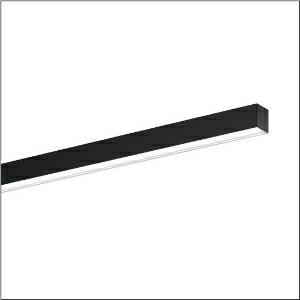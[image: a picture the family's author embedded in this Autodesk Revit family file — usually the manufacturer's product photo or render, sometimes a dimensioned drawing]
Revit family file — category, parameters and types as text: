
# Revit family: silica_21_51mx20db32bb
name_source: partatom
category: Lighting Fixtures
units: mm (PartAtom-declared; Revit-internal decimal feet)

## family parameters
Cut with Voids When Loaded = No
Host = Face
Light Source = No
Part Type = Normal
Room Calculation Point = No
Round Connector Dimension = Use Diameter
Shared = No

## types (1)
- --- (1 x LED, 3000 lm, 20.2 W, 3000K)
    Apparent Load = 20 VA
    CIE Flux Codes = 48 79 96 100 100
    Color Rendering = 80
    Color Temperature = 3000K
    Default Elevation = 1800 mm
    Description = Silica 21, office luminaire, primary optical cover: cover, of PMMA, opal, light emission: direct distribution, primary light characteristic: symmetric, installation type: surface-mounted, LED, rated luminous flux: 3.000lm, luminous efficacy: 149lm/W, light colour: 830, colour temperature: 3000K, control gear: DALI 2, with terminal, 3+2-pole, max. 2.5mm², mains connection: 220..240V, AC, 50/60Hz, luminaire housing, of aluminium, matt jet black (RAL 9005), length: 1.504mm, width: 53mm, height: 53mm, protection rating (complete): IP20, insulation class (complete): insulation class I (protective earthing), certification: CE, permissible operating ambient temperature: 0..+35°C, standard: EN 50419, packaging unit: 1 piece
    Height = 53 mm
    Lamp = 1 x LED
    Lamp Light Flux = 3000 lm
    Lamp Power = 20.2 W
    Lamp count = 1
    Length = 1504 mm
    Luminous efficacy = 149 lm/W
    Manufacturer = Siteco
    ModVariant = No
    Model = 51MX20DB32BB
    Mounting Place = Ceiling
    Mounting Type = Surface mounted
    Number of Poles = 1
    OnlyDefault = Yes
    Power Factor = 1
    Product Name = Silica 21
    Product group = office luminaire | ceiling mounted
    ProductGroupID = 301
    Protection Class = Protection class I
    Protection Degree = IP 20
    RLX_Detail_Level = 1
    RLX_Emergency_Light_Flux = 0 lm
    RLX_Emergency_Type = 0
    RLX_Emergency_Type_DB = No
    RlxData = <blob elided: 28621 chars, md5=acfb19ae>
    Socket = socket
    Standby Power = 0 W
    System Light Flux = 3000 lm
    System Power = 20 W
    Type Comments = factory setting: luminous flux: 100 % | dim-lin: 254 | 233 mA
    Type Image = l_1335925.jpg
    URL = http://relux.com
    VarID = @adj_118217
    Voltage = 0 V
    Weight = 0.00 kg
    Width = 53 mm

## geometry (parser evidence)
native form markers: Blend x4, Sweep x12
no freeform markers — native parametric forms only
